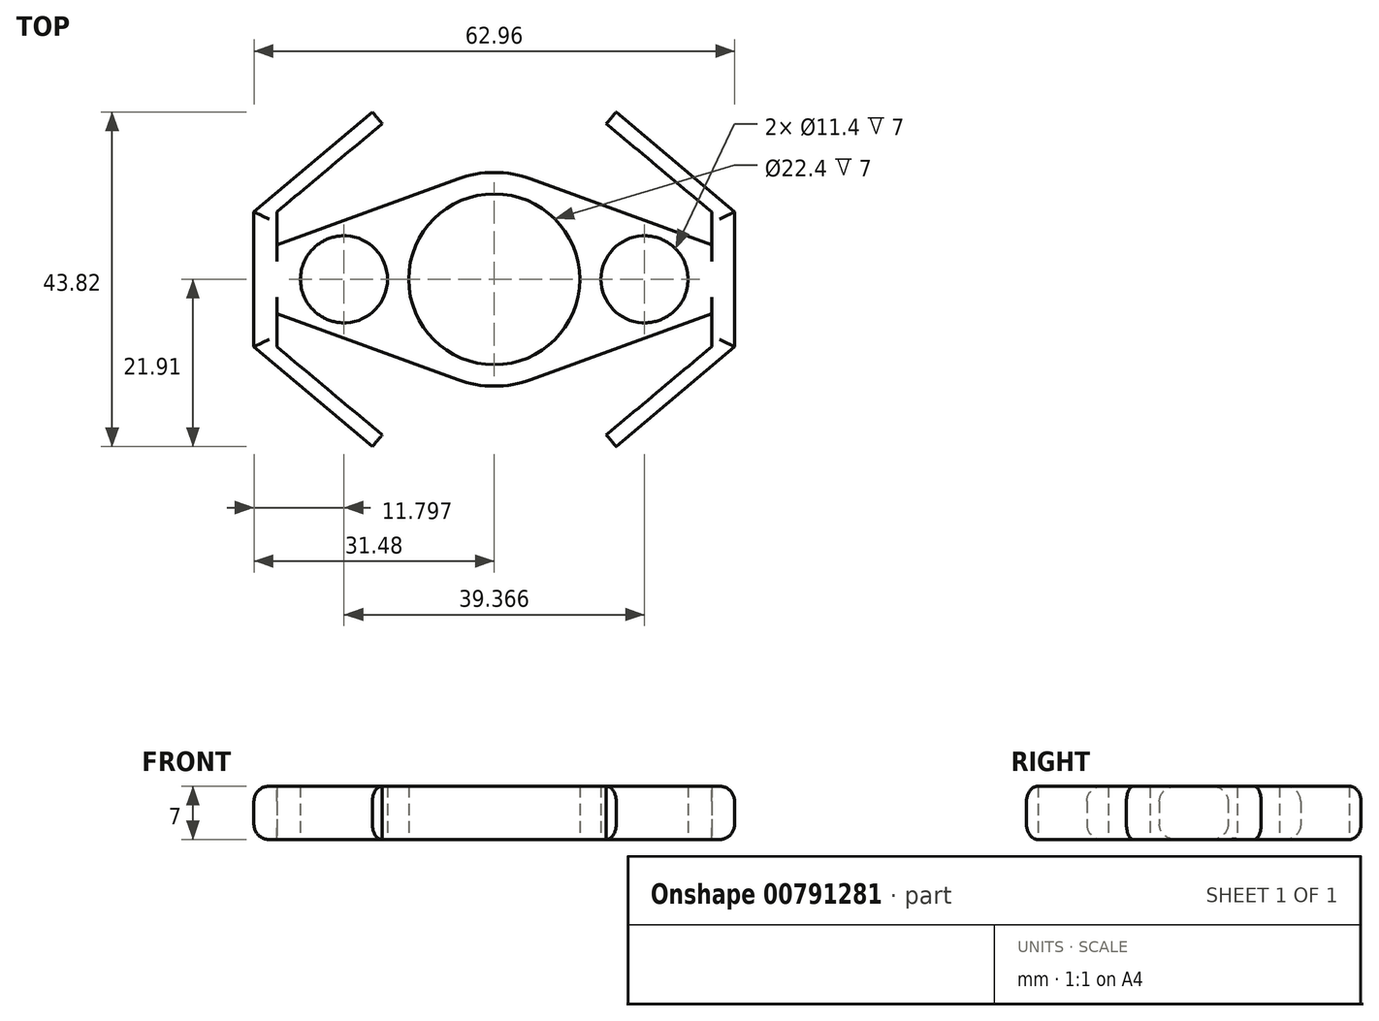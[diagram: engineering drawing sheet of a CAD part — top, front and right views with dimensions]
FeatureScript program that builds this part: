
annotation { "Feature Type Name" : "Feature", "Feature Type Description" : "" }
export const myFeature = defineFeature(function(context is Context, id is Id, definition is map)
    precondition{}
    {
        {
            var Q0;
            Q0=qCreatedBy(makeId("Top.planeOp"),FACE);
            var sketch = newSketch(context, id + "F0", { "sketchPlane" : qUnion([Q0])});
            skCircle(sketch, "E0", {"center": v(0, 0) * mm, "radius": 11.2 * mm});
            skArc(sketch, "E1", {"start": v(-4.8, -13.15) * mm, "mid": v(0, -14) * mm, "end": v(4.8, -13.15) * mm});
            skLineSegment(sketch, "E2", {"start": v(28.48, 4.5) * mm, "end": v(4.8, 13.15) * mm});
            skLineSegment(sketch, "E3", {"start": v(28.48, -4.5) * mm, "end": v(4.8, -13.15) * mm});
            skCircle(sketch, "E4", {"center": v(19.68, 0) * mm, "radius": 5.7 * mm});
            skLineSegment(sketch, "E5.1.0", {"start": v(-28.48, -4.5) * mm, "end": v(-4.8, -13.15) * mm});
            skLineSegment(sketch, "E5.1.1", {"start": v(-28.48, 4.5) * mm, "end": v(-4.8, 13.15) * mm});
            skCircle(sketch, "E6.1.0", {"center": v(-19.68, 0) * mm, "radius": 5.7 * mm});
            skLineSegment(sketch, "E7", {"start": v(28.48, 8.82) * mm, "end": v(28.48, 4.5) * mm});
            skLineSegment(sketch, "E8", {"start": v(31.48, 8.82) * mm, "end": v(31.48, -8.82) * mm});
            skLineSegment(sketch, "E9.1.0", {"start": v(-31.48, -8.82) * mm, "end": v(-31.48, 8.82) * mm});
            skLineSegment(sketch, "E9.1.2", {"start": v(-28.48, -8.82) * mm, "end": v(-28.48, -4.5) * mm});
            skPoint(sketch, "E10.orphan", {"position": v(-40.78, 0) * mm});
            skLineSegment(sketch, "E11.trimOffspring", {"start": v(-28.48, 4.5) * mm, "end": v(-28.48, 8.82) * mm});
            skLineSegment(sketch, "E12.trimOffspring", {"start": v(28.48, -4.5) * mm, "end": v(28.48, -8.82) * mm});
            skArc(sketch, "E13.trimOffspring", {"start": v(4.8, 13.15) * mm, "mid": v(0, 14) * mm, "end": v(-4.8, 13.15) * mm});
            skLineSegment(sketch, "E14.MirrorCS", {"start": v(-28.48, 8.82) * mm, "end": v(-28.48, 4.5) * mm});
            skLineSegment(sketch, "E15.MirrorCS", {"start": v(-28.48, -4.5) * mm, "end": v(-28.48, -8.82) * mm});
            skLineSegment(sketch, "E16", {"start": v(-28.48, 8.82) * mm, "end": v(-14.68, 20.38) * mm});
            skLineSegment(sketch, "E17", {"start": v(-14.68, 20.38) * mm, "end": v(-15.97, 21.91) * mm});
            skLineSegment(sketch, "E18", {"start": v(-15.97, 21.91) * mm, "end": v(-31.48, 8.82) * mm});
            skLineSegment(sketch, "E19.MirrorCS", {"start": v(-15.97, -21.91) * mm, "end": v(-31.48, -8.82) * mm});
            skLineSegment(sketch, "E20.MirrorCS", {"start": v(-28.48, -8.82) * mm, "end": v(-14.68, -20.38) * mm});
            skLineSegment(sketch, "E21.MirrorCS", {"start": v(-14.68, -20.38) * mm, "end": v(-15.97, -21.91) * mm});
            skLineSegment(sketch, "E22.MirrorCS", {"start": v(15.97, 21.91) * mm, "end": v(31.48, 8.82) * mm});
            skLineSegment(sketch, "E23.MirrorCS", {"start": v(28.48, 8.82) * mm, "end": v(14.68, 20.38) * mm});
            skLineSegment(sketch, "E24.MirrorCS", {"start": v(14.68, 20.38) * mm, "end": v(15.97, 21.91) * mm});
            skLineSegment(sketch, "E25.MirrorCS", {"start": v(28.48, -8.82) * mm, "end": v(14.68, -20.38) * mm});
            skLineSegment(sketch, "E26.MirrorCS", {"start": v(15.97, -21.91) * mm, "end": v(31.48, -8.82) * mm});
            skLineSegment(sketch, "E27", {"start": v(14.68, -20.38) * mm, "end": v(15.97, -21.91) * mm});
            skSolve(sketch);
        }
        {
            var Q0;
            Q0=makeQuery(id+"F0.imprint","IMPRINT",FACE,{"disambiguationData":[TD([[makeQuery(id+"F0.imprint","IMPRINT",EDGE,{"derivedFrom":sQuery(id+"F0.wireOp",EDGE,"E0")}),-1.0]])]});
            extrude(context, id + "F1", {"entities" : qUnion([Q0]), "depth" : 7 * mm, "offsetDistance" : 25 * mm});
        }
        {
            var Q0;
            Q0=makeQuery(id+"F1.opExtrude","CAP_EDGE",EDGE,{"disambiguationData":[OSD([sQuery(id+"F0.wireOp",EDGE,"E5.1.0")])],"isStart":false});
            var Q1;
            Q1=makeQuery(id+"F1.opExtrude","CAP_EDGE",EDGE,{"disambiguationData":[OSD([sQuery(id+"F0.wireOp",EDGE,"E5.1.1")])],"isStart":false});
            var Q2;
            Q2=makeQuery(id+"F1.opExtrude","CAP_EDGE",EDGE,{"disambiguationData":[OSD([sQuery(id+"F0.wireOp",EDGE,"E3")])],"isStart":true});
            var Q3;
            Q3=makeQuery(id+"F1.opExtrude","CAP_EDGE",EDGE,{"disambiguationData":[OSD([sQuery(id+"F0.wireOp",EDGE,"E2")])],"isStart":true});
            var Q4;
            Q4=makeQuery(id+"F1.opExtrude","CAP_EDGE",EDGE,{"disambiguationData":[OSD([sQuery(id+"F0.wireOp",EDGE,"E22.MirrorCS")])],"isStart":false});
            var Q5;
            Q5=makeQuery(id+"F1.opExtrude","CAP_EDGE",EDGE,{"disambiguationData":[OSD([sQuery(id+"F0.wireOp",EDGE,"E22.MirrorCS")])],"isStart":true});
            var Q6;
            Q6=makeQuery(id+"F1.opExtrude","CAP_EDGE",EDGE,{"disambiguationData":[OSD([sQuery(id+"F0.wireOp",EDGE,"E8")])],"isStart":false});
            var Q7;
            Q7=makeQuery(id+"F1.opExtrude","CAP_EDGE",EDGE,{"disambiguationData":[OSD([sQuery(id+"F0.wireOp",EDGE,"E8")])],"isStart":true});
            var Q8;
            Q8=makeQuery(id+"F1.opExtrude","CAP_EDGE",EDGE,{"disambiguationData":[OSD([sQuery(id+"F0.wireOp",EDGE,"E26.MirrorCS")])],"isStart":false});
            var Q9;
            Q9=makeQuery(id+"F1.opExtrude","CAP_EDGE",EDGE,{"disambiguationData":[OSD([sQuery(id+"F0.wireOp",EDGE,"E26.MirrorCS")])],"isStart":true});
            var Q10;
            Q10=makeQuery(id+"F1.opExtrude","CAP_EDGE",EDGE,{"disambiguationData":[OSD([sQuery(id+"F0.wireOp",EDGE,"E18")])],"isStart":false});
            var Q11;
            Q11=makeQuery(id+"F1.opExtrude","CAP_EDGE",EDGE,{"disambiguationData":[OSD([sQuery(id+"F0.wireOp",EDGE,"E9.1.0")])],"isStart":false});
            var Q12;
            Q12=makeQuery(id+"F1.opExtrude","CAP_EDGE",EDGE,{"disambiguationData":[OSD([sQuery(id+"F0.wireOp",EDGE,"E19.MirrorCS")])],"isStart":false});
            var Q13;
            Q13=makeQuery(id+"F1.opExtrude","CAP_EDGE",EDGE,{"disambiguationData":[OSD([sQuery(id+"F0.wireOp",EDGE,"E19.MirrorCS")])],"isStart":true});
            var Q14;
            Q14=makeQuery(id+"F1.opExtrude","CAP_EDGE",EDGE,{"disambiguationData":[OSD([sQuery(id+"F0.wireOp",EDGE,"E9.1.0")])],"isStart":true});
            var Q15;
            Q15=makeQuery(id+"F1.opExtrude","CAP_EDGE",EDGE,{"disambiguationData":[OSD([sQuery(id+"F0.wireOp",EDGE,"E18")])],"isStart":true});
            fillet(context, id + "F2", {"entities" : qUnion([Q0, Q1, Q2, Q3, Q4, Q5, Q6, Q7, Q8, Q9, Q10, Q11, Q12, Q13, Q14, Q15]), "radius" : 2 * mm, "tangentPropagation" : true, "allowEdgeOverflow" : false});
        }
    });
